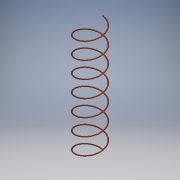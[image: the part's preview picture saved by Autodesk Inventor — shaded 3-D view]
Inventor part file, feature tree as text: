
AUTODESK INVENTOR PART (.ipt)
format: ipt  version: 2018 (Build 220112000, 112)  size: 277,504 bytes
history: native  units: mm
features: helix x1, sketch x1
ambient origin geometry x8: Origin, YZ Plane, XZ Plane, XY Plane, X Axis, Y Axis, Z Axis, Center Point
bodies: Solid1 (feature_tree)
feature tree (2):
  helix  "Coil1"  [1 undecoded]
  sketch  "Sketch1"  dims[d1=7.8994mm d2=237.3mm d3=158.6mm d4=158.6mm d5=10.0mm d6=70.0mm d7=0.0mm d8=90.0deg d9=90.0deg d10=0.0mm d11=0.0mm]
note: 1 required parameter value undecoded (feature->parameter linkage not recoverable at this tier; creation-order binding heuristic only, values carry confidence <= 0.55)
